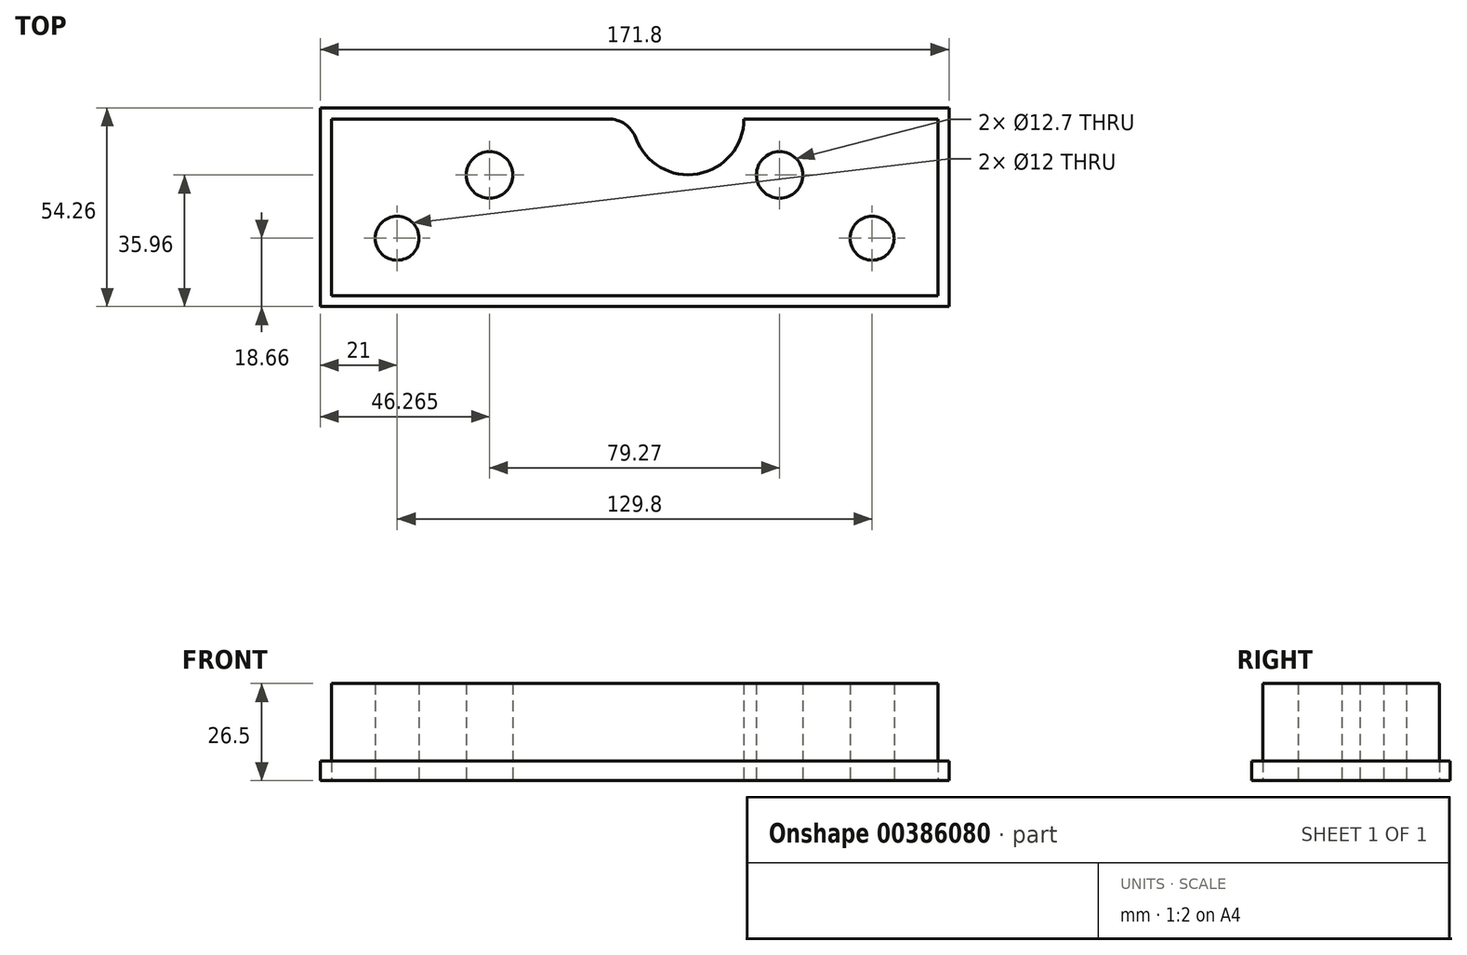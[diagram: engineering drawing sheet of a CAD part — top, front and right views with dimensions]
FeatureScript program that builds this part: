
annotation { "Feature Type Name" : "Feature", "Feature Type Description" : "" }
export const myFeature = defineFeature(function(context is Context, id is Id, definition is map)
    precondition{}
    {
        {
            var Q0;
            Q0=qCreatedBy(makeId("Top.planeOp"),FACE);
            var sketch = newSketch(context, id + "F0", { "sketchPlane" : qUnion([Q0])});
            skLineSegment(sketch, "E0.bottom", {"start": v(-82.9, 32.6) * mm, "end": v(-7.18, 32.6) * mm});
            skLineSegment(sketch, "E0.top", {"start": v(-82.9, -15.66) * mm, "end": v(82.9, -15.66) * mm});
            skLineSegment(sketch, "E0.left", {"start": v(-82.9, 32.6) * mm, "end": v(-82.9, -15.66) * mm});
            skLineSegment(sketch, "E0.right", {"start": v(82.9, 32.6) * mm, "end": v(82.9, -15.66) * mm});
            skCircle(sketch, "E1", {"center": v(-39.63, 17.3) * mm, "radius": 6.35 * mm});
            skCircle(sketch, "E2", {"center": v(39.63, 17.3) * mm, "radius": 6.35 * mm});
            skCircle(sketch, "E3", {"center": v(64.9, 0) * mm, "radius": 6 * mm});
            skCircle(sketch, "E4", {"center": v(-64.9, 0) * mm, "radius": 6 * mm});
            skPoint(sketch, "E5", {"position": v(-70.9, 0) * mm});
            skPoint(sketch, "E6", {"position": v(70.9, 0) * mm});
            skPoint(sketch, "E7", {"position": v(-58.9, 0) * mm});
            skPoint(sketch, "E8", {"position": v(58.9, 0) * mm});
            skPoint(sketch, "E9", {"position": v(-45.98, 17.3) * mm});
            skPoint(sketch, "E10", {"position": v(45.98, 17.3) * mm});
            skPoint(sketch, "E11", {"position": v(-33.28, 17.3) * mm});
            skPoint(sketch, "E12", {"position": v(33.28, 17.3) * mm});
            skArc(sketch, "E13", {"start": v(0.33, 27.35) * mm, "mid": v(17.3, 17.6) * mm, "end": v(29.87, 32.6) * mm});
            skLineSegment(sketch, "E14", {"start": v(-39.63, 17.3) * mm, "end": v(39.63, 17.3) * mm, "construction": true});
            skLineSegment(sketch, "E15", {"start": v(64.9, 0) * mm, "end": v(-64.9, 0) * mm, "construction": true});
            skLineSegment(sketch, "E16", {"start": v(0, 0) * mm, "end": v(0, 17.3) * mm, "construction": true});
            skLineSegment(sketch, "E17", {"start": v(-0.6, 32.6) * mm, "end": v(29.87, 32.6) * mm, "construction": true});
            skLineSegment(sketch, "E18", {"start": v(29.87, 32.6) * mm, "end": v(82.9, 32.6) * mm});
            skPoint(sketch, "E19.visualSharp", {"position": v(-0.6, 32.6) * mm});
            skArc(sketch, "E19.filletArc", {"start": v(0.33, 27.35) * mm, "mid": v(-2.6, 31.16) * mm, "end": v(-7.18, 32.6) * mm});
            skSolve(sketch);
        }
        {
            var Q0;
            Q0=makeQuery(id+"F0.imprint","IMPRINT",FACE,{"disambiguationData":[TD([[makeQuery(id+"F0.imprint","IMPRINT",EDGE,{"derivedFrom":sQuery(id+"F0.wireOp",EDGE,"E0.top")}),1.0]])]});
            extrude(context, id + "F1", {"entities" : qUnion([Q0]), "depth" : 26.5 * mm});
        }
        {
            var Q0;
            Q0=qCreatedBy(makeId("Top.planeOp"),FACE);
            var sketch = newSketch(context, id + "F2", { "sketchPlane" : qUnion([Q0])});
            skPoint(sketch, "E20.0", {"position": v(-82.9, 32.6) * mm});
            skPoint(sketch, "E21.0", {"position": v(-82.9, -15.66) * mm});
            skPoint(sketch, "E22.0", {"position": v(82.9, -15.66) * mm});
            skLineSegment(sketch, "E23.bottom", {"start": v(-85.9, -18.66) * mm, "end": v(85.9, -18.66) * mm});
            skLineSegment(sketch, "E23.top", {"start": v(-85.9, 35.6) * mm, "end": v(85.9, 35.6) * mm});
            skLineSegment(sketch, "E23.left", {"start": v(-85.9, -18.66) * mm, "end": v(-85.9, 35.6) * mm});
            skLineSegment(sketch, "E23.right", {"start": v(85.9, -18.66) * mm, "end": v(85.9, 35.6) * mm});
            skSolve(sketch);
        }
        {
            var Q0;
            Q0=makeQuery(id+"F2.imprint","IMPRINT",FACE,{"disambiguationData":[TD([[makeQuery(id+"F2.imprint","IMPRINT",EDGE,{"derivedFrom":sQuery(id+"F2.wireOp",EDGE,"E23.bottom")}),1.0]])]});
            extrude(context, id + "F3", {"entities" : qUnion([Q0]), "depth" : 5.3 * mm});
        }
    });
